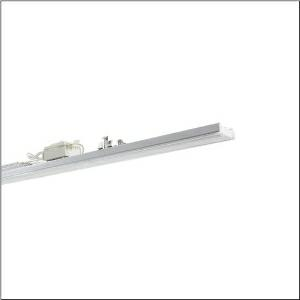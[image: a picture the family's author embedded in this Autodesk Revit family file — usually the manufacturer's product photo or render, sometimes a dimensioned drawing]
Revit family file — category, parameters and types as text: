
# Revit family: licross_r__21_recessed_mo_52te12dv3dxg_0489
name_source: partatom
category: Lighting Fixtures
units: mm (PartAtom-declared; Revit-internal decimal feet)

## family parameters
Cut with Voids When Loaded = No
Host = Face
Light Source = No
Part Type = Normal
Room Calculation Point = No
Round Connector Dimension = Use Diameter
Shared = No

## types (1)
- --- (1 x LED, 13000 lm, 76.1 W, 3000K)
    Apparent Load = 76 VA
    CIE Flux Codes = 72 92 99 100 100
    Color Rendering = 80
    Color Temperature = 3000K
    Default Elevation = 1800 mm
    Description = Licross® 21 Recessed MO, luminaire insert, of sheet steel, galvanised, coil coated, white, length: 2.250mm, width: 66mm, height: 67mm, LED rated luminous flux: 13.000lm, light colour: 830, control gear: DALI 2, with plug, 5-pole, with phase selection, mains connection: 220..240V, AC, 50/60Hz, rated input power: 76W, halogen-free wiring, primary optical cover: cover, of PMMA, light emission: direct distribution, primary light characteristic: symmetric, protection rating (complete): IP54, insulation class (complete): insulation class I (protective earthing), certification: CE, ENEC, VDE, UKCA, protection symbol: D if used in an environment with non-conductive dust loads with corresponding accessories, impact resistance: IK06, permissible ambient temperature for indoor applications: -25..+35°C, corresponds to IFS (International Featured Standards) requirements for safety and quality in the food industry, reducing of maximum allowable ambient temperature of 5°C with ceiling mounting, LABS conformity tested according to VDMA 24364:2018-05, packaging unit: 1 piece
    Height = 58 mm
    Lamp = 1 x LED
    Lamp Light Flux = 13000 lm
    Lamp Power = 76.1 W
    Lamp count = 1
    Length = 2250 mm
    Luminous efficacy = 171 lm/W
    Manufacturer = Siteco
    ModVariant = No
    Model = 52TE12DV3DXG
    Mounting Place = Ceiling
    Mounting Type = Pendant
    Number of Poles = 1
    OnlyDefault = Yes
    Power Factor = 1
    Product Name = Licross® 21 Recessed MO
    Product group = luminaire insert
    ProductGroupID = 902
    Protection Class = Protection class I
    Protection Degree = IP 54
    RLX_Detail_Level = 1
    RLX_Emergency_Light_Flux = 0 lm
    RLX_Emergency_Type = 0
    RLX_Emergency_Type_DB = No
    RlxData = <blob elided: 29549 chars, md5=36dc762c>
    Socket = socket
    Standby Power = 0 W
    System Light Flux = 13000 lm
    System Power = 76 W
    Type Comments = factory setting: luminous flux: 100 % | dim-lin: 254 | 347 mA
    Type Image = l_1296930.jpg
    URL = http://relux.com
    VarID = @adj_032576
    Voltage = 0 V
    Weight = 0.00 kg
    Width = 66 mm

## geometry (parser evidence)
native form markers: Blend x4, Sweep x10
no freeform markers — native parametric forms only
